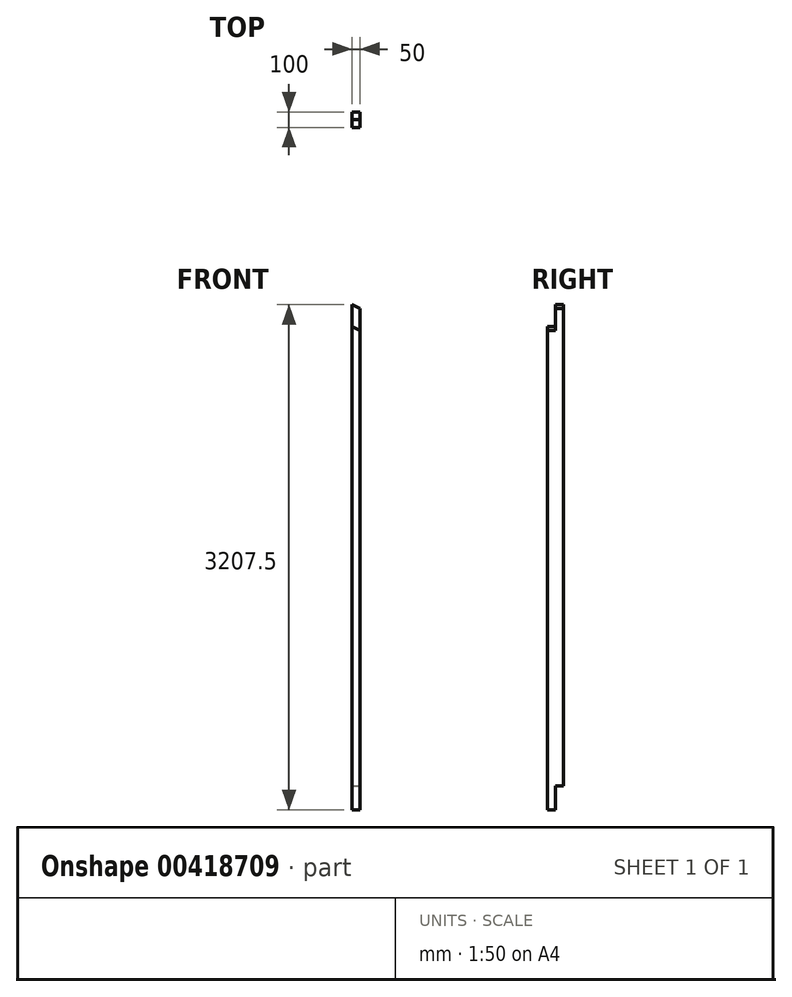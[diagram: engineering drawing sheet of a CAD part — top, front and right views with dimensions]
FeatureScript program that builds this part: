
annotation { "Feature Type Name" : "Feature", "Feature Type Description" : "" }
export const myFeature = defineFeature(function(context is Context, id is Id, definition is map)
    precondition{}
    {
        {
            var Q0;
            Q0=qCreatedBy(makeId("Top.planeOp"),FACE);
            var sketch = newSketch(context, id + "F0", { "sketchPlane" : qUnion([Q0])});
            skLineSegment(sketch, "E0.bottom", {"start": v(-25, 50) * mm, "end": v(25, 50) * mm});
            skLineSegment(sketch, "E0.top", {"start": v(-25, -50) * mm, "end": v(25, -50) * mm});
            skLineSegment(sketch, "E0.left", {"start": v(-25, 50) * mm, "end": v(-25, -50) * mm});
            skLineSegment(sketch, "E0.right", {"start": v(25, 50) * mm, "end": v(25, -50) * mm});
            skPoint(sketch, "E0.middle", {"position": v(0, 0) * mm});
            skSolve(sketch);
        }
        {
            var Q0;
            Q0=qSketchRegion(id+"F0",true);
            extrude(context, id + "F1", {"entities" : qUnion([Q0]), "depth" : (3210 - 2.5) * mm});
        }
        {
            var Q0;
            Q0=qCreatedBy(makeId("Right.planeOp"),FACE);
            var sketch = newSketch(context, id + "F2", { "sketchPlane" : qUnion([Q0])});
            skLineSegment(sketch, "E1.bottom", {"start": v(50, 0) * mm, "end": v(0, 0) * mm});
            skLineSegment(sketch, "E1.top", {"start": v(50, 150) * mm, "end": v(0, 150) * mm});
            skLineSegment(sketch, "E1.left", {"start": v(50, 0) * mm, "end": v(50, 150) * mm});
            skLineSegment(sketch, "E1.right", {"start": v(0, 0) * mm, "end": v(0, 150) * mm});
            skSolve(sketch);
        }
        {
            var Q0;
            Q0=qSketchRegion(id+"F2",true);
            extrude(context, id + "F3", {"entities" : qUnion([Q0]), "operationType" : NewBodyOperationType.REMOVE, "endBound" : BoundingType.UP_TO_NEXT, "oppositeDirection" : true, "depth" : 25 * mm, "hasSecondDirection" : true, "secondDirectionBound" : SecondDirectionBoundingType.UP_TO_NEXT, "secondDirectionOppositeDirection" : false, "secondDirectionDepth" : 25 * mm});
        }
        {
            var Q0;
            Q0=makeQuery(id+"F1.opExtrude","SWEPT_FACE",FACE,{"disambiguationData":[OSD([sQuery(id+"F0.wireOp",EDGE,"E0.top")])]});
            var sketch = newSketch(context, id + "F4", { "sketchPlane" : qUnion([Q0])});
            skLineSegment(sketch, "E2", {"start": v(-25, 3207.5) * mm, "end": v(25, 3182.5) * mm});
            skLineSegment(sketch, "E3", {"start": v(25, 3182.5) * mm, "end": v(25, 3207.5) * mm});
            skLineSegment(sketch, "E4", {"start": v(25, 3207.5) * mm, "end": v(-25, 3207.5) * mm});
            skSolve(sketch);
        }
        {
            var Q0;
            Q0=qSketchRegion(id+"F4",true);
            extrude(context, id + "F5", {"entities" : qUnion([Q0]), "operationType" : NewBodyOperationType.REMOVE, "endBound" : BoundingType.UP_TO_NEXT, "oppositeDirection" : true, "depth" : 25 * mm});
        }
        {
            var Q0;
            Q0=makeQuery(id+"F1.opExtrude","SWEPT_FACE",FACE,{"disambiguationData":[OSD([sQuery(id+"F0.wireOp",EDGE,"E0.top")])]});
            var sketch = newSketch(context, id + "F6", { "sketchPlane" : qUnion([Q0])});
            skLineSegment(sketch, "E5", {"start": v(-25, 3207.5) * mm, "end": v(25, 3182.5) * mm});
            skLineSegment(sketch, "E6", {"start": v(25, 3182.5) * mm, "end": v(25, 3042.75) * mm});
            skLineSegment(sketch, "E7", {"start": v(25, 3042.75) * mm, "end": v(-25, 3067.75) * mm});
            skLineSegment(sketch, "E8", {"start": v(-25, 3067.75) * mm, "end": v(-25, 3207.5) * mm});
            skSolve(sketch);
        }
        {
            var Q0;
            Q0=qSketchRegion(id+"F6",true);
            extrude(context, id + "F7", {"entities" : qUnion([Q0]), "operationType" : NewBodyOperationType.REMOVE, "oppositeDirection" : true, "depth" : 50 * mm});
        }
    });
